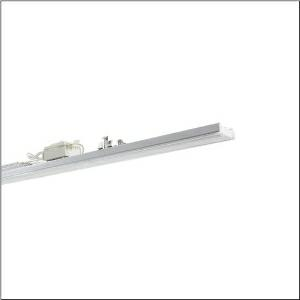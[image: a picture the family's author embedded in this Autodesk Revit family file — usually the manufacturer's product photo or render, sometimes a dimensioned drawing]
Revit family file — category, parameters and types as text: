
# Revit family: licross_r__11_recessed_mo_51tl18dv48xg_1c4d
name_source: partatom
category: Lighting Fixtures
units: mm (PartAtom-declared; Revit-internal decimal feet)

## family parameters
Cut with Voids When Loaded = No
Host = Face
Light Source = No
Part Type = Normal
Room Calculation Point = No
Round Connector Dimension = Use Diameter
Shared = No

## types (1)
- --- (1 x LED, 8000 lm, 43.2 W, 4000K)
    Apparent Load = 43 VA
    CIE Flux Codes = 83 96 99 100 100
    Color Rendering = 80
    Color Temperature = 4000K
    Default Elevation = 1800 mm
    Description = Licross® 11 Recessed MO, luminaire insert, of sheet steel, coil coated, white, length: 2.250mm, width: 66mm, height: 67mm, LED rated luminous flux: 8.000lm, light colour: 840, control gear: DALI 2, with plug, 5-pole, with phase selection, mains connection: 220..240V, AC, 50/60Hz, rated input power: 43W, internal wiring halogen-free, primary light control with lens, of plastic, primary optical cover: cover, of PMMA, light emission: direct distribution, primary light characteristic: symmetric, protection rating (complete): IP40, insulation class (complete): insulation class I (protective earthing), certification: CE, ENEC, VDE, UKCA, protection symbol: D if used in an environment without relevant dust loads with corresponding accessories, impact resistance: IK06, permissible ambient temperature for indoor applications: -25..+45°C, corresponds to IFS (International Featured Standards) requirements for safety and quality in the food industry, reducing of maximum allowable ambient temperature of 5°C with ceiling mounting, LABS conformity tested according to VDMA 24364:2018-05, packaging unit: 1 piece
    Height = 58 mm
    Lamp = 1 x LED
    Lamp Light Flux = 8000 lm
    Lamp Power = 43.2 W
    Lamp count = 1
    Length = 2250 mm
    Luminous efficacy = 185 lm/W
    Manufacturer = Siteco
    ModVariant = No
    Model = 51TL18DV48XG
    Mounting Place = Ceiling
    Mounting Type = Pendant
    Number of Poles = 1
    OnlyDefault = Yes
    Power Factor = 1
    Product Name = Licross® 11 Recessed MO
    Product group = luminaire insert | ceiling pendant
    ProductGroupID = 902
    Protection Class = Protection class I
    Protection Degree = IP 40
    RLX_Detail_Level = 1
    RLX_Emergency_Light_Flux = 0 lm
    RLX_Emergency_Type = 0
    RLX_Emergency_Type_DB = No
    RlxData = <blob elided: 29249 chars, md5=de981da3>
    Socket = socket
    Standby Power = 0 W
    System Light Flux = 8000 lm
    System Power = 43 W
    Type Comments = factory setting: luminous flux: 100 % | dim-lin: 254 | 194 mA
    Type Image = l_1296930.jpg
    URL = http://relux.com
    VarID = @adj_120545
    Voltage = 0 V
    Weight = 0.00 kg
    Width = 66 mm

## geometry (parser evidence)
native form markers: Blend x4, Sweep x9
no freeform markers — native parametric forms only
